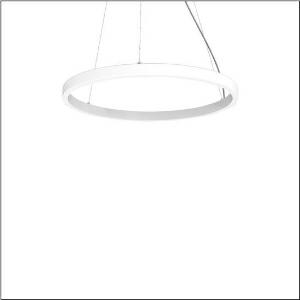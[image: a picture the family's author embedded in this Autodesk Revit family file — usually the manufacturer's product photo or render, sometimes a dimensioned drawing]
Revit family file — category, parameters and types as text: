
# Revit family: silica_21_ring-o_5pjbo3d3004a
name_source: partatom
category: Lighting Fixtures
units: mm (PartAtom-declared; Revit-internal decimal feet)

## family parameters
Cut with Voids When Loaded = No
Host = Face
Light Source = No
Part Type = Normal
Room Calculation Point = No
Round Connector Dimension = Use Diameter
Shared = No

## types (1)
- Silica 21 Ring-O (1 x LED, 7210 lm, 105 W, 4000K)
    Apparent Load = 105 VA
    CIE Flux Codes = 2 16 49 50 100
    Color Rendering = 80
    Color Temperature = 4000K
    Default Elevation = 1800 mm
    Description = Silica 21 Ring-O, suspended luminaire, of PMMA, frosted, light emission: outer ring side luminous distribution, primary light characteristic: symmetric, installation type: suspended mounting, LED, rated luminous flux: 7.210lm, luminous efficacy: 69lm/W, light colour: 840, colour temperature: 4000K, control gear: DALI 2, with terminal, 5-pole, mains connection: 230V, AC/DC, 0/50..60Hz, rated input power: 105W, housing, of extruded aluminium section, traffic white (RAL 9016), diameter: 1.100mm, ceiling canopy, traffic white (RAL 9016), protection rating (lamp compartment): IP40, insulation class (complete): insulation class I (protective earthing), certification: CE, impact resistance: IK02, permissible operating ambient temperature: 0..+35°C, packaging unit: 1 piece
    Height = 48 mm  [stored 0.15748 ft]
    Lamp = 1 x LED
    Lamp Light Flux = 7210 lm
    Lamp Power = 105 W
    Lamp count = 1
    Length = 1100 mm
    Luminous efficacy = 69 lm/W
    Manufacturer = Siteco
    ModVariant = No
    Model = 5PJBO3D3004A
    Mounting Place = Ceiling
    Mounting Type = Pendant
    Number of Poles = 1
    OnlyDefault = Yes
    Power Factor = 1
    Product Name = Silica 21 Ring-O
    Product group = suspended luminaire
    ProductGroupID = 904
    Protection Class = Protection class I
    Protection Degree = IP 40
    RLX_Detail_Level = 1
    RLX_Emergency_Light_Flux = 0 lm
    RLX_Emergency_Type = 0
    RLX_Emergency_Type_DB = No
    RlxData = <blob elided: 13521 chars, md5=30fc6860>
    Socket = socket
    Standby Power = 0 W
    System Light Flux = 7210 lm
    System Power = 105 W
    Type Comments = Product without accessories
    Type Image = l_1258387.jpg
    URL = http://relux.com
    VarID = ---
    Voltage = 0 V
    Weight = 0.00 kg
    Width = 0 mm  [stored 0 ft]

note: [stored X ft] marks values corroborated as IEEE doubles in the binary element streams (Revit-internal decimal feet)

## geometry (parser evidence)
native form markers: Sweep x12
no freeform markers — native parametric forms only
